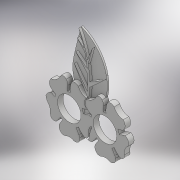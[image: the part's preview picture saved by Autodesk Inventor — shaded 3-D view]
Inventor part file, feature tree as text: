
AUTODESK INVENTOR PART (.ipt)
format: ipt  version: 2017 (Build 210142000, 142)  size: 376,832 bytes
history: native  units: mm
features: extrude x3, sketch x3, projected_geometry x1
ambient origin geometry x8: Origin, YZ Plane, XZ Plane, XY Plane, X Axis, Y Axis, Z Axis, Center Point
bodies: Solid1 (feature_tree)
feature tree (7):
  extrude  "Extrusion1"  Depth=4.0mm
  extrude  "Extrusion3"  Depth=3.0mm TaperAngle=0.0deg
  extrude  "Extrusion4"  [1 undecoded]
  sketch  "Sketch1"  dims[d0=17.0mm d1=17.0mm d2=21.0mm d3=21.0mm d4=4.0mm d5=0.0mm d6=35.0mm]
  sketch  "Sketch4"  dims[d11=1.2mm d12=0.0mm d13=3.0mm d14=0.0mm]
  sketch  "Sketch5"
  projected_geometry  "Projected Loop2"
note: 1 required parameter value undecoded (feature->parameter linkage not recoverable at this tier; creation-order binding heuristic only, values carry confidence <= 0.55)
